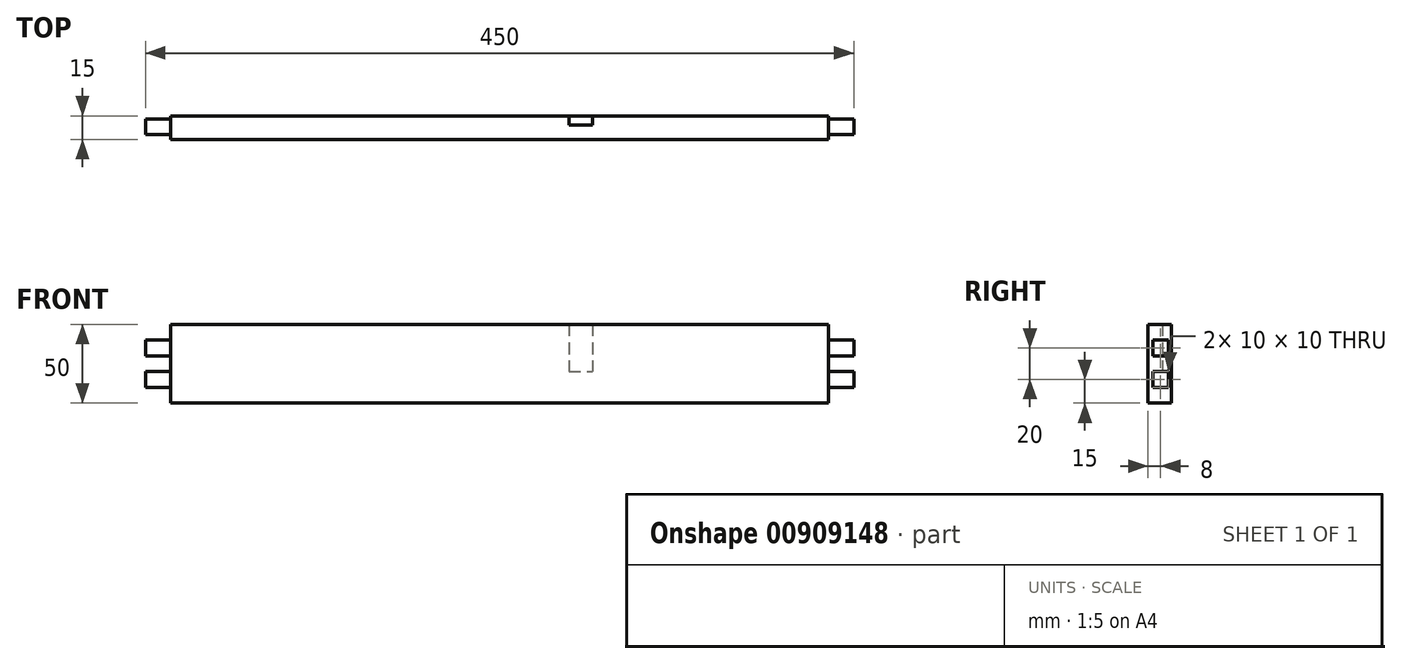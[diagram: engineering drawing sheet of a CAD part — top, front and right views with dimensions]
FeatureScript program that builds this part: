
annotation { "Feature Type Name" : "Feature", "Feature Type Description" : "" }
export const myFeature = defineFeature(function(context is Context, id is Id, definition is map)
    precondition{}
    {
        {
            var Q0;
            Q0=qCreatedBy(makeId("Front.planeOp"),FACE);
            var sketch = newSketch(context, id + "F0", { "sketchPlane" : qUnion([Q0])});
            skLineSegment(sketch, "E0.bottom", {"start": v(209, -25) * mm, "end": v(-209, -25) * mm});
            skLineSegment(sketch, "E0.top", {"start": v(209, 25) * mm, "end": v(-209, 25) * mm});
            skLineSegment(sketch, "E0.left", {"start": v(209, -25) * mm, "end": v(209, 25) * mm});
            skLineSegment(sketch, "E0.right", {"start": v(-209, -25) * mm, "end": v(-209, 25) * mm});
            skPoint(sketch, "E0.middle", {"position": v(0, 0) * mm});
            skSolve(sketch);
        }
        {
            var Q0;
            Q0=makeQuery(id+"F0.imprint","IMPRINT",FACE,{"disambiguationData":[TD([[makeQuery(id+"F0.imprint","IMPRINT",EDGE,{"derivedFrom":sQuery(id+"F0.wireOp",EDGE,"E0.bottom")}),-1.0]])]});
            extrude(context, id + "F1", {"entities" : qUnion([Q0]), "depth" : 15 * mm, "offsetDistance" : 25 * mm});
        }
        {
            var Q0;
            Q0=makeQuery(id+"F1.opExtrude","SWEPT_FACE",FACE,{"disambiguationData":[OSD([sQuery(id+"F0.wireOp",EDGE,"E0.left")])]});
            var sketch = newSketch(context, id + "F2", { "sketchPlane" : qUnion([Q0])});
            skLineSegment(sketch, "E1", {"start": v(-12, 15) * mm, "end": v(-12, 5) * mm});
            skLineSegment(sketch, "E2", {"start": v(-12, 5) * mm, "end": v(-2, 5) * mm});
            skLineSegment(sketch, "E3", {"start": v(-2, 5) * mm, "end": v(-2, 15) * mm});
            skLineSegment(sketch, "E4", {"start": v(-2, -15) * mm, "end": v(-2, -5) * mm});
            skLineSegment(sketch, "E5", {"start": v(-2, -5) * mm, "end": v(-12, -5) * mm});
            skLineSegment(sketch, "E6", {"start": v(-12, -5) * mm, "end": v(-12, -15) * mm});
            skLineSegment(sketch, "E7", {"start": v(-12, 15) * mm, "end": v(-2, 15) * mm});
            skLineSegment(sketch, "E8", {"start": v(-12, -15) * mm, "end": v(-2, -15) * mm});
            skSolve(sketch);
        }
        {
            var Q0;
            Q0=makeQuery(id+"F2.imprint","IMPRINT",FACE,{"disambiguationData":[TD([[makeQuery(id+"F2.imprint","IMPRINT",EDGE,{"derivedFrom":sQuery(id+"F2.wireOp",EDGE,"1h3BVDke-zrxr-6g8v-9iLc-erCNEwpC3fz9.bottom")}),-1.0]])]});
            var Q1;
            Q1=makeQuery(id+"F2.imprint","IMPRINT",FACE,{"disambiguationData":[TD([[makeQuery(id+"F2.imprint","IMPRINT",EDGE,{"derivedFrom":sQuery(id+"F2.wireOp",EDGE,"E1")}),1.0]])]});
            var Q2;
            Q2=makeQuery(id+"F2.imprint","IMPRINT",FACE,{"disambiguationData":[TD([[makeQuery(id+"F2.imprint","IMPRINT",EDGE,{"derivedFrom":sQuery(id+"F2.wireOp",EDGE,"E4")}),1.0]])]});
            extrude(context, id + "F3", {"entities" : qUnion([Q0, Q1, Q2]), "operationType" : NewBodyOperationType.ADD, "depth" : 16 * mm, "offsetDistance" : 25 * mm});
        }
        {
            var Q0;
            Q0=makeQuery(id+"F1.opExtrude","SWEPT_FACE",FACE,{"disambiguationData":[OSD([sQuery(id+"F0.wireOp",EDGE,"E0.right")])]});
            var sketch = newSketch(context, id + "F4", { "sketchPlane" : qUnion([Q0])});
            skLineSegment(sketch, "E9", {"start": v(2, 5) * mm, "end": v(12, 5) * mm});
            skLineSegment(sketch, "E10", {"start": v(2, -5) * mm, "end": v(12, -5) * mm});
            skLineSegment(sketch, "E11", {"start": v(2, 15) * mm, "end": v(12, 15) * mm});
            skLineSegment(sketch, "E12", {"start": v(12, -15) * mm, "end": v(2, -15) * mm});
            skLineSegment(sketch, "E13", {"start": v(2, 15) * mm, "end": v(2, 5) * mm});
            skLineSegment(sketch, "E14", {"start": v(12, 15) * mm, "end": v(12, 5) * mm});
            skLineSegment(sketch, "E15", {"start": v(12, -5) * mm, "end": v(12, -15) * mm});
            skLineSegment(sketch, "E16", {"start": v(2, -5) * mm, "end": v(2, -15) * mm});
            skSolve(sketch);
        }
        {
            var Q0;
            Q0=makeQuery(id+"F4.imprint","IMPRINT",FACE,{"disambiguationData":[TD([[makeQuery(id+"F4.imprint","IMPRINT",EDGE,{"derivedFrom":sQuery(id+"F4.wireOp",EDGE,"E9")}),1.0]])]});
            var Q1;
            Q1=makeQuery(id+"F4.imprint","IMPRINT",FACE,{"disambiguationData":[TD([[makeQuery(id+"F4.imprint","IMPRINT",EDGE,{"derivedFrom":sQuery(id+"F4.wireOp",EDGE,"E10")}),-1.0]])]});
            extrude(context, id + "F5", {"entities" : qUnion([Q0, Q1]), "operationType" : NewBodyOperationType.ADD, "depth" : 16 * mm, "offsetDistance" : 25 * mm});
        }
        {
            var Q0;
            Q0=makeQuery(id+"F0.imprint","IMPRINT",FACE,{"disambiguationData":[TD([[makeQuery(id+"F0.imprint","IMPRINT",EDGE,{"derivedFrom":sQuery(id+"F0.wireOp",EDGE,"E0.bottom")}),-1.0]])]});
            var sketch = newSketch(context, id + "F6", { "sketchPlane" : qUnion([Q0])});
            skLineSegment(sketch, "E17.bottom", {"start": v(59, 25) * mm, "end": v(44, 25) * mm});
            skLineSegment(sketch, "E18", {"start": v(59, 25) * mm, "end": v(59, -5) * mm});
            skLineSegment(sketch, "E19", {"start": v(44, 25) * mm, "end": v(44, -5) * mm});
            skLineSegment(sketch, "E20", {"start": v(44, -5) * mm, "end": v(59, -5) * mm});
            skSolve(sketch);
        }
        {
            var Q0;
            Q0=makeQuery(id+"F6.imprint","IMPRINT",FACE,{"disambiguationData":[TD([[makeQuery(id+"F6.imprint","IMPRINT",EDGE,{"derivedFrom":sQuery(id+"F6.wireOp",EDGE,"E17.bottom")}),1.0]])]});
            extrude(context, id + "F7", {"entities" : qUnion([Q0]), "operationType" : NewBodyOperationType.REMOVE, "depth" : 6 * mm, "offsetDistance" : 25 * mm});
        }
    });
